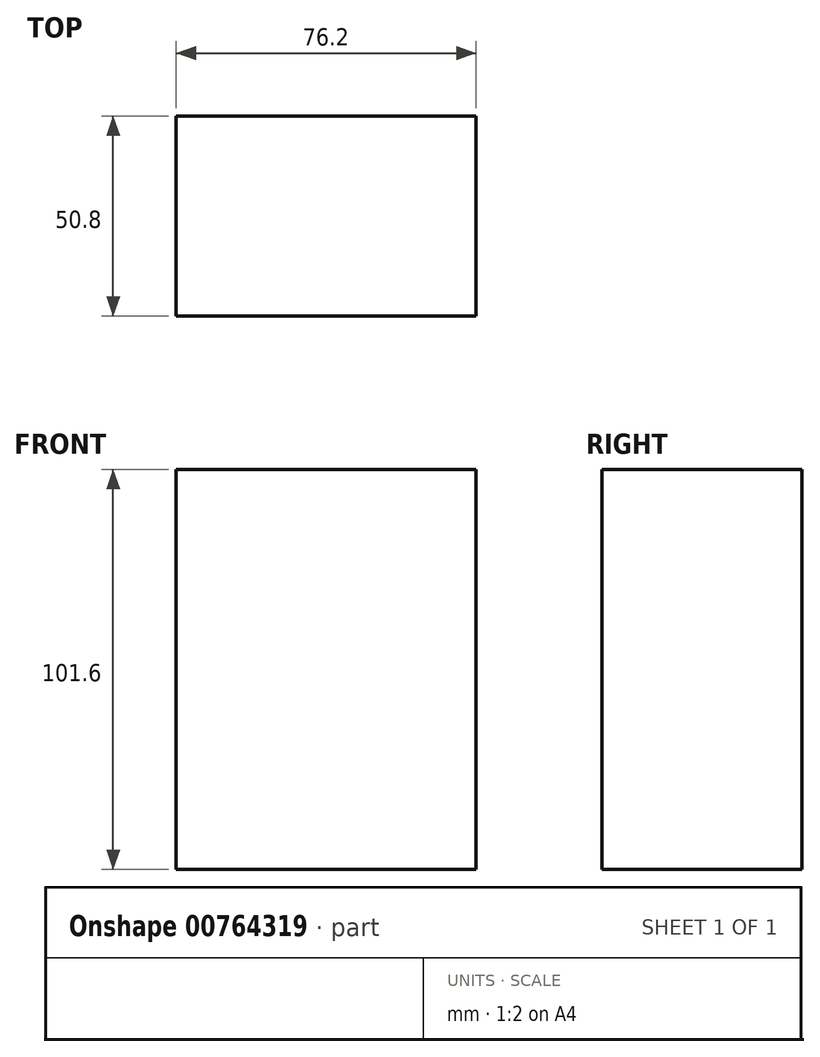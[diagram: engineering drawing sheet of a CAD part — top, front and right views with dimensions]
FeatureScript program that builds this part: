
annotation { "Feature Type Name" : "Feature", "Feature Type Description" : "" }
export const myFeature = defineFeature(function(context is Context, id is Id, definition is map)
    precondition{}
    {
        {
            var Q0;
            Q0=qCreatedBy(makeId("Top.planeOp"),FACE);
            var sketch = newSketch(context, id + "F0", { "sketchPlane" : qUnion([Q0])});
            skLineSegment(sketch, "E0.bottom", {"start": v(-116.6, 0) * mm, "end": v(-40.4, 0) * mm});
            skLineSegment(sketch, "E0.top", {"start": v(-116.6, 50.8) * mm, "end": v(-40.4, 50.8) * mm});
            skLineSegment(sketch, "E0.left", {"start": v(-116.6, 0) * mm, "end": v(-116.6, 50.8) * mm});
            skLineSegment(sketch, "E0.right", {"start": v(-40.4, 0) * mm, "end": v(-40.4, 50.8) * mm});
            skSolve(sketch);
        }
        {
            var Q0;
            Q0=makeQuery(id+"F0.imprint","IMPRINT",FACE,{"disambiguationData":[TD([[makeQuery(id+"F0.imprint","IMPRINT",EDGE,{"derivedFrom":sQuery(id+"F0.wireOp",EDGE,"E0.bottom")}),1.0]])]});
            extrude(context, id + "F1", {"entities" : qUnion([Q0]), "depth" : 101.6 * mm, "offsetDistance" : 25.4 * mm});
        }
    });
